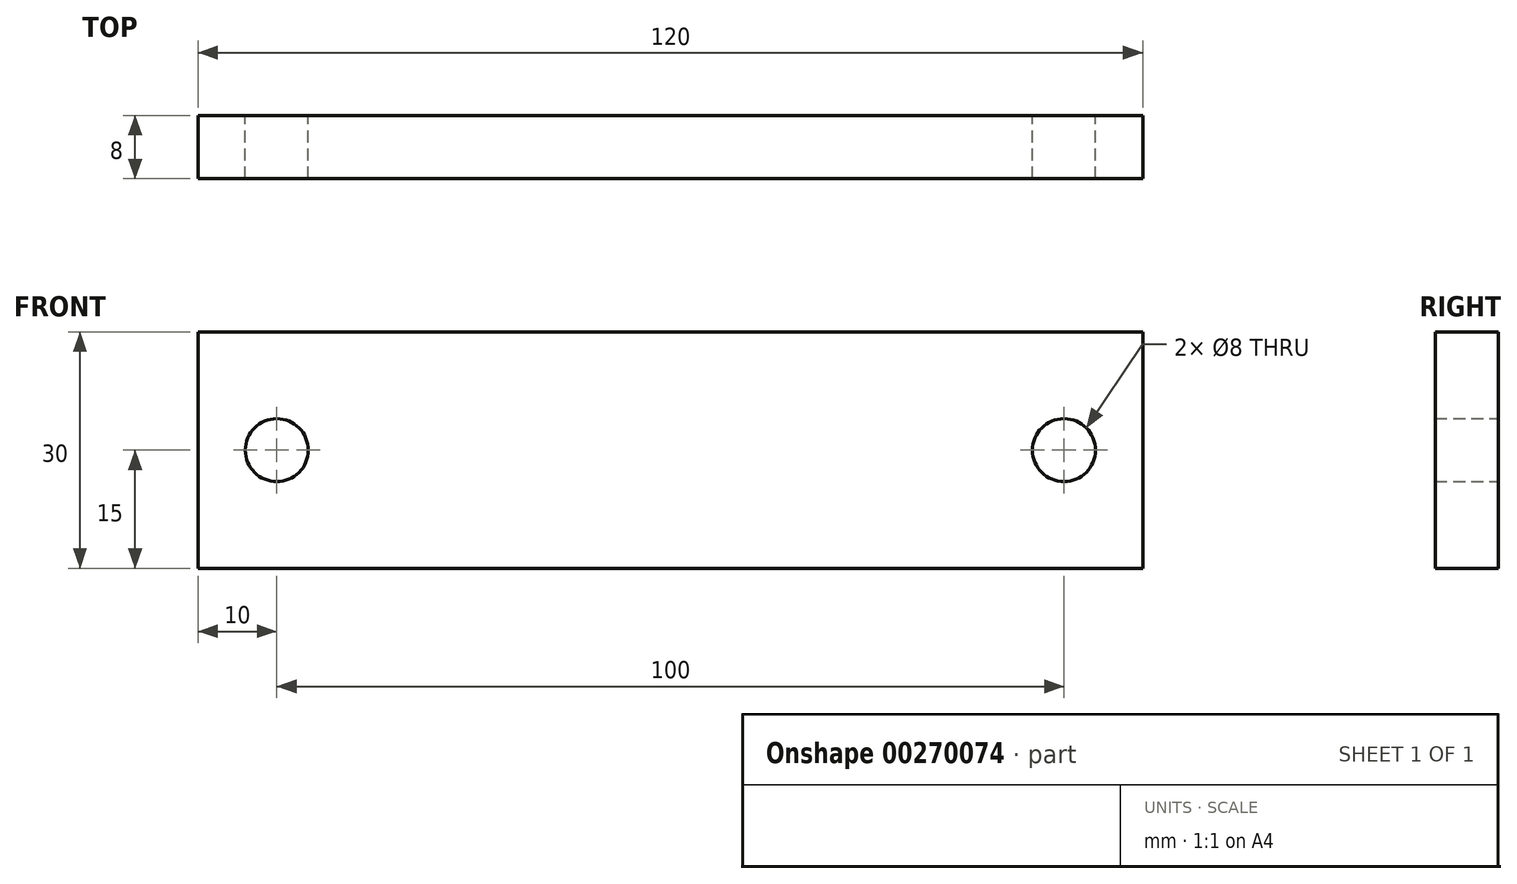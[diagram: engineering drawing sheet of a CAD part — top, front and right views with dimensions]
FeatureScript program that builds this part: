
annotation { "Feature Type Name" : "Feature", "Feature Type Description" : "" }
export const myFeature = defineFeature(function(context is Context, id is Id, definition is map)
    precondition{}
    {
        {
            var Q0;
            Q0=qCreatedBy(makeId("Front.planeOp"),FACE);
            var sketch = newSketch(context, id + "F0", { "sketchPlane" : qUnion([Q0])});
            skLineSegment(sketch, "E0.bottom", {"start": v(60, 15) * mm, "end": v(-60, 15) * mm});
            skLineSegment(sketch, "E0.top", {"start": v(60, -15) * mm, "end": v(-60, -15) * mm});
            skLineSegment(sketch, "E0.left", {"start": v(60, 15) * mm, "end": v(60, -15) * mm});
            skLineSegment(sketch, "E0.right", {"start": v(-60, 15) * mm, "end": v(-60, -15) * mm});
            skPoint(sketch, "E0.middle", {"position": v(0, 0) * mm});
            skCircle(sketch, "E1", {"center": v(-50, 0) * mm, "radius": 4 * mm});
            skPoint(sketch, "E1.centerSnap0", {"position": v(-60, 0) * mm});
            skCircle(sketch, "E2", {"center": v(50, 0) * mm, "radius": 4 * mm});
            skPoint(sketch, "E2.centerSnap0", {"position": v(60, 0) * mm});
            skSolve(sketch);
        }
        {
            var Q0;
            Q0=makeQuery(id+"F0.imprint","IMPRINT",FACE,{"disambiguationData":[TD([[makeQuery(id+"F0.imprint","IMPRINT",EDGE,{"derivedFrom":sQuery(id+"F0.wireOp",EDGE,"E0.bottom")}),1.0]])]});
            extrude(context, id + "F1", {"entities" : qUnion([Q0]), "depth" : 8 * mm});
        }
    });
